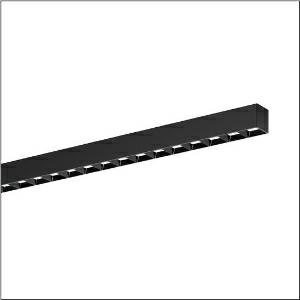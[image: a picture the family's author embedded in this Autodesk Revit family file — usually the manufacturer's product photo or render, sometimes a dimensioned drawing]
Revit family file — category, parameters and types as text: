
# Revit family: silica_21_51mx21tctab
name_source: partatom
category: Lighting Fixtures
units: mm (PartAtom-declared; Revit-internal decimal feet)

## family parameters
Cut with Voids When Loaded = No
Host = Face
Light Source = No
Part Type = Normal
Room Calculation Point = No
Round Connector Dimension = Use Diameter
Shared = No

## types (1)
- --- (1 x LED, 9300 lm, 80.5 W, 6500K)
    Apparent Load = 81 VA
    CIE Flux Codes = 85 99 100 100 100
    Color Rendering = 80
    Color Temperature = 6500K
    Default Elevation = 1800 mm
    Description = Silica 21, office luminaire, primary light control with darklight reflector, of PMMA, black, CAT 2 (L<= 3000cd/m²), light emission: direct distribution, primary light characteristic: symmetric, installation type: surface-mounted, LED, rated luminous flux: 9.300lm, luminous efficacy: 110lm/W, light colour: 8tw, colour temperature: 2700..6500K, control gear: DALI DT8, with terminal, 3+2-pole, max. 2.5mm², mains connection: 220..240V, AC, 50/60Hz, rated input power: 84.6W, luminaire housing, of aluminium, matt jet black (RAL 9005), length: 3.004mm, width: 53mm, height: 53mm, protection rating (complete): IP20, insulation class (complete): insulation class I (protective earthing), certification: CE, permissible operating ambient temperature: 0..+35°C, standard: EN 50419, packaging unit: 1 piece
    Height = 53 mm
    Lamp = 1 x LED
    Lamp Light Flux = 9300 lm
    Lamp Power = 80.5 W
    Lamp count = 1
    Length = 3004 mm
    Luminous efficacy = 116 lm/W
    Manufacturer = Siteco
    ModVariant = No
    Model = 51MX21TCTAB
    Mounting Place = Ceiling
    Mounting Type = Surface mounted
    Number of Poles = 1
    OnlyDefault = Yes
    Power Factor = 1
    Product Name = Silica 21
    Product group = office luminaire | ceiling mounted
    ProductGroupID = 301
    Protection Class = Protection class I
    Protection Degree = IP 20
    RLX_Detail_Level = 1
    RLX_Emergency_Light_Flux = 0 lm
    RLX_Emergency_Type = 0
    RLX_Emergency_Type_DB = No
    RlxData = <blob elided: 60973 chars, md5=140ceafe>
    Socket = socket
    Standby Power = 0 W
    System Light Flux = 9300 lm
    System Power = 81 W
    Type Comments = individual setting
    Type Image = l_1335908.jpg
    URL = http://relux.com
    VarID = @adj_139553
    Voltage = 0 V
    Weight = 0.00 kg
    Width = 53 mm

## geometry (parser evidence)
native form markers: Blend x4, Sweep x10
no freeform markers — native parametric forms only
